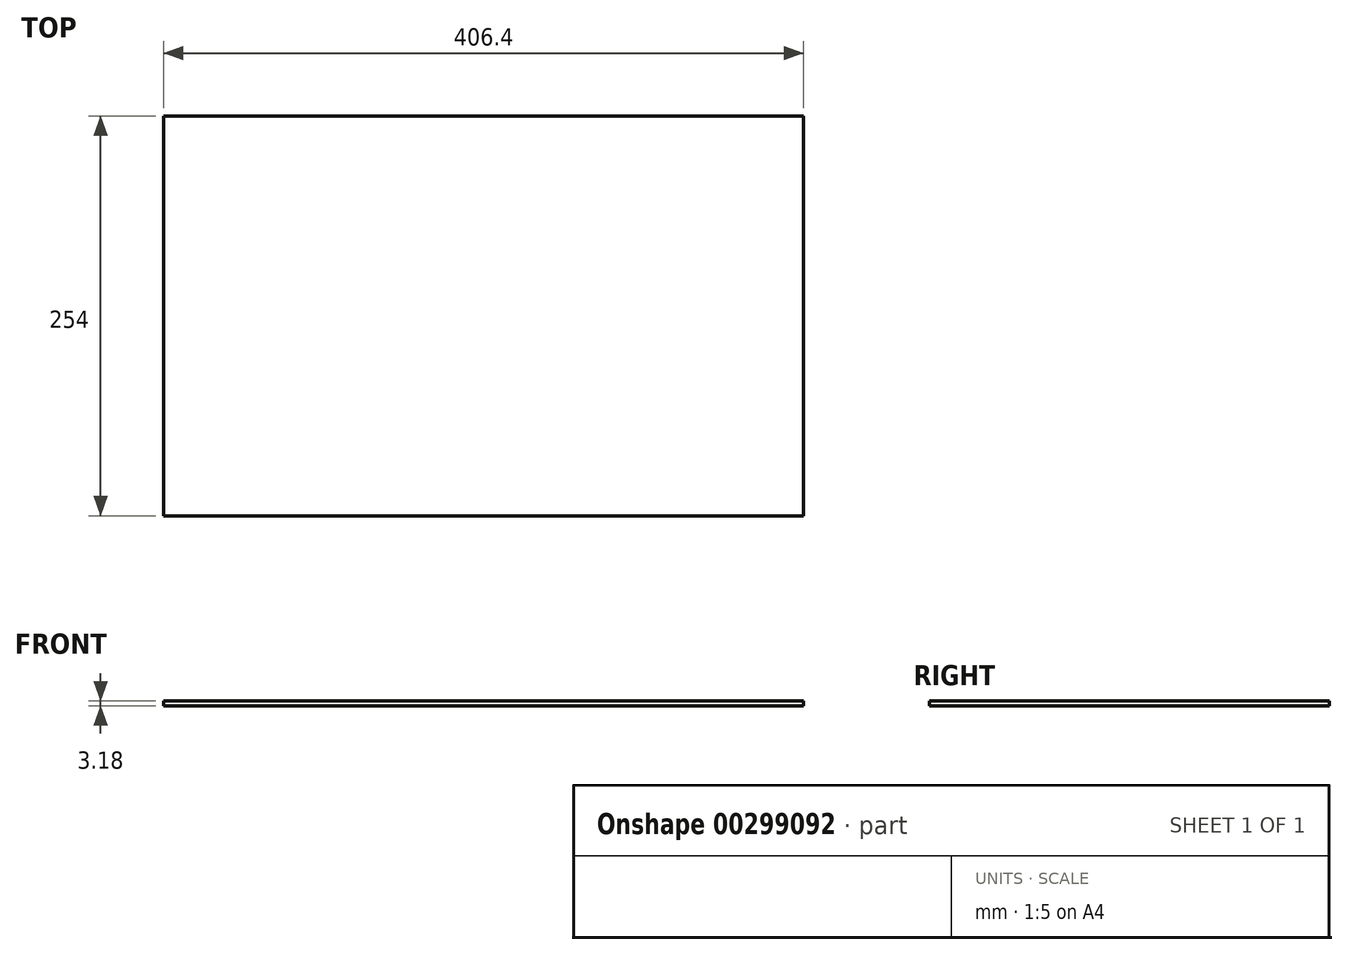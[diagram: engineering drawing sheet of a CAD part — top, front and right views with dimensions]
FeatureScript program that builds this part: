
annotation { "Feature Type Name" : "Feature", "Feature Type Description" : "" }
export const myFeature = defineFeature(function(context is Context, id is Id, definition is map)
    precondition{}
    {
        {
            var Q0;
            Q0=qCreatedBy(makeId("Top.planeOp"),FACE);
            var sketch = newSketch(context, id + "F0", { "sketchPlane" : qUnion([Q0])});
            skLineSegment(sketch, "E0.bottom", {"start": v(-203.2, 127) * mm, "end": v(203.2, 127) * mm});
            skLineSegment(sketch, "E0.top", {"start": v(-203.2, -127) * mm, "end": v(203.2, -127) * mm});
            skLineSegment(sketch, "E0.left", {"start": v(-203.2, 127) * mm, "end": v(-203.2, -127) * mm});
            skLineSegment(sketch, "E0.right", {"start": v(203.2, 127) * mm, "end": v(203.2, -127) * mm});
            skPoint(sketch, "E0.middle", {"position": v(0, 0) * mm});
            skSolve(sketch);
        }
        {
            var Q0;
            Q0 = qSketchRegion(id + "F0", true);
            extrude(context, id + "F1", {"entities" : qUnion([Q0]), "endBound" : BoundingType.SYMMETRIC, "depth" : 3.17 * mm});
        }
    });
